# Revit family: CL10033-C_CLARK ROUND SQUARE WALL MIXER WITH DIVERTER
name_source: partatom
category: Plumbing Fixtures
revit_build: Autodesk Revit 2015 (Build: 20140606_1530(x64)
units: mm (PartAtom-declared; Revit-internal decimal feet)

## types (2) — shared parameters
Assembly Code = C1030220
CW Connection = Yes
Default Elevation = 900 mm  [stored 2.95276 ft]
Description = CLARK ROUND SQUARE WALL MIXER WITH DIVERTER
HW Connection = Yes
Manufacturer = GWA Bathrooms & Kitchens
URL = https://www.clark.com.au
Vent Connection = No
Waste Connection = No

## per-type parameters (varying)
| type | Material_Base | Model |
| CLARK ROUND SQUARE WALL MIXER WITH DIVERTER - Chrome | GWA_Metal-Chrome | CL10033.C |
| CLARK ROUND SQUARE WALL MIXER WITH DIVERTER - Black | GWA-Metal-Black | CL10033.B |

note: [stored X ft] marks values corroborated as IEEE doubles in the binary element streams (Revit-internal decimal feet)

## geometry (parser evidence)
native form markers: Sweep x2
no freeform markers — native parametric forms only
